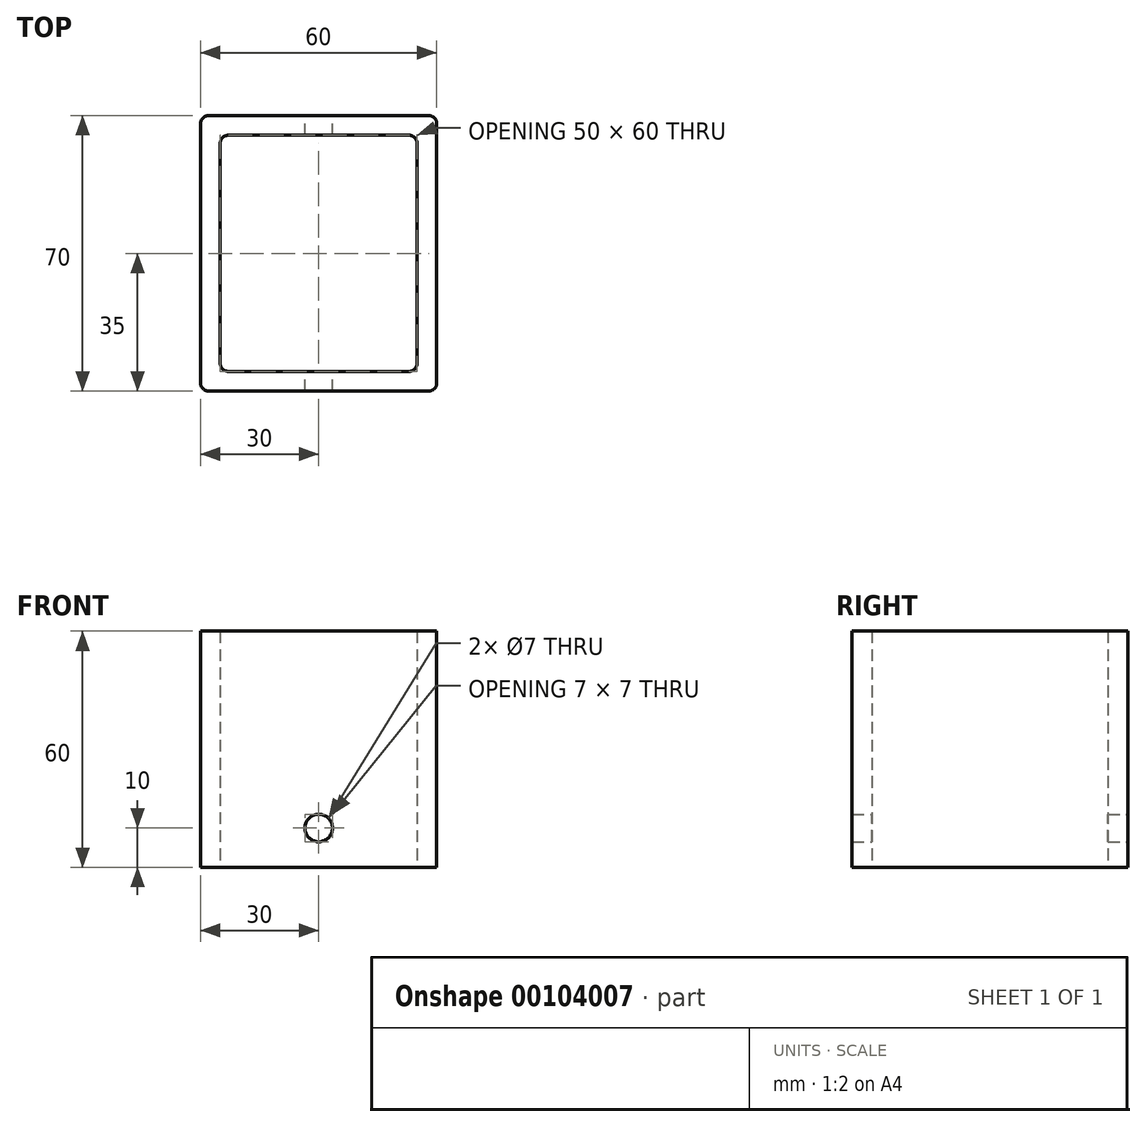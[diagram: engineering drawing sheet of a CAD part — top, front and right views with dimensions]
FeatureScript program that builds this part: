
annotation { "Feature Type Name" : "Feature", "Feature Type Description" : "" }
export const myFeature = defineFeature(function(context is Context, id is Id, definition is map)
    precondition{}
    {
        {
            var Q0;
            Q0=qCreatedBy(makeId("Top.planeOp"),FACE);
            var sketch = newSketch(context, id + "F0", { "sketchPlane" : qUnion([Q0])});
            skLineSegment(sketch, "E0.bottom", {"start": v(30, -35) * mm, "end": v(-30, -35) * mm});
            skLineSegment(sketch, "E0.top", {"start": v(30, 35) * mm, "end": v(-30, 35) * mm});
            skLineSegment(sketch, "E0.left", {"start": v(30, -35) * mm, "end": v(30, 35) * mm});
            skLineSegment(sketch, "E0.right", {"start": v(-30, -35) * mm, "end": v(-30, 35) * mm});
            skPoint(sketch, "E0.middle", {"position": v(0, 0) * mm});
            skLineSegment(sketch, "E1.bottom", {"start": v(25, -30) * mm, "end": v(-25, -30) * mm});
            skLineSegment(sketch, "E1.top", {"start": v(25, 30) * mm, "end": v(-25, 30) * mm});
            skLineSegment(sketch, "E1.left", {"start": v(25, -30) * mm, "end": v(25, 30) * mm});
            skLineSegment(sketch, "E1.right", {"start": v(-25, -30) * mm, "end": v(-25, 30) * mm});
            skSolve(sketch);
        }
        {
            var Q0;
            Q0=makeQuery(id+"F0.imprint","IMPRINT",FACE,{"disambiguationData":[TD([[makeQuery(id+"F0.imprint","IMPRINT",EDGE,{"derivedFrom":sQuery(id+"F0.wireOp",EDGE,"E0.bottom")}),-1.0]])]});
            extrude(context, id + "F1", {"entities" : qUnion([Q0]), "depth" : 60 * mm});
        }
        {
            var Q0;
            Q0=makeQuery(id+"F1.opExtrude","SWEPT_EDGE",EDGE,{"disambiguationData":[OSD([sQuery(id+"F0.wireOp",EDGE,"E0.top"),sQuery(id+"F0.wireOp",EDGE,"E0.right")])]});
            var Q1;
            Q1=makeQuery(id+"F1.opExtrude","SWEPT_EDGE",EDGE,{"disambiguationData":[OSD([sQuery(id+"F0.wireOp",EDGE,"E0.top"),sQuery(id+"F0.wireOp",EDGE,"E0.left")])]});
            var Q2;
            Q2=makeQuery(id+"F1.opExtrude","SWEPT_EDGE",EDGE,{"disambiguationData":[OSD([sQuery(id+"F0.wireOp",EDGE,"E0.bottom"),sQuery(id+"F0.wireOp",EDGE,"E0.left")])]});
            var Q3;
            Q3=makeQuery(id+"F1.opExtrude","SWEPT_EDGE",EDGE,{"disambiguationData":[OSD([sQuery(id+"F0.wireOp",EDGE,"E0.bottom"),sQuery(id+"F0.wireOp",EDGE,"E0.right")])]});
            var Q4;
            Q4=makeQuery(id+"F1.opExtrude","SWEPT_EDGE",EDGE,{"disambiguationData":[OSD([sQuery(id+"F0.wireOp",EDGE,"E1.top"),sQuery(id+"F0.wireOp",EDGE,"E1.right")])]});
            var Q5;
            Q5=makeQuery(id+"F1.opExtrude","SWEPT_EDGE",EDGE,{"disambiguationData":[OSD([sQuery(id+"F0.wireOp",EDGE,"E1.top"),sQuery(id+"F0.wireOp",EDGE,"E1.left")])]});
            var Q6;
            Q6=makeQuery(id+"F1.opExtrude","SWEPT_EDGE",EDGE,{"disambiguationData":[OSD([sQuery(id+"F0.wireOp",EDGE,"E1.bottom"),sQuery(id+"F0.wireOp",EDGE,"E1.right")])]});
            var Q7;
            Q7=makeQuery(id+"F1.opExtrude","SWEPT_EDGE",EDGE,{"disambiguationData":[OSD([sQuery(id+"F0.wireOp",EDGE,"E1.bottom"),sQuery(id+"F0.wireOp",EDGE,"E1.left")])]});
            fillet(context, id + "F2", {"entities" : qUnion([Q0, Q1, Q2, Q3, Q4, Q5, Q6, Q7]), "radius" : 2 * mm, "tangentPropagation" : true, "allowEdgeOverflow" : false});
        }
        {
            var Q0;
            Q0=makeQuery(id+"F1.opExtrude","SWEPT_FACE",FACE,{"disambiguationData":[OSD([sQuery(id+"F0.wireOp",EDGE,"E0.top")])]});
            var sketch = newSketch(context, id + "F3", { "sketchPlane" : qUnion([Q0])});
            skCircle(sketch, "E2", {"center": v(0, 10) * mm, "radius": 3.5 * mm});
            skSolve(sketch);
        }
        {
            var Q0;
            Q0=makeQuery(id+"F3.imprint","IMPRINT",FACE,{"disambiguationData":[TD([[makeQuery(id+"F3.imprint","IMPRINT",EDGE,{"derivedFrom":sQuery(id+"F3.wireOp",EDGE,"E2")}),1.0]])]});
            extrude(context, id + "F4", {"entities" : qUnion([Q0]), "operationType" : NewBodyOperationType.REMOVE, "oppositeDirection" : true, "depth" : 70 * mm});
        }
    });
